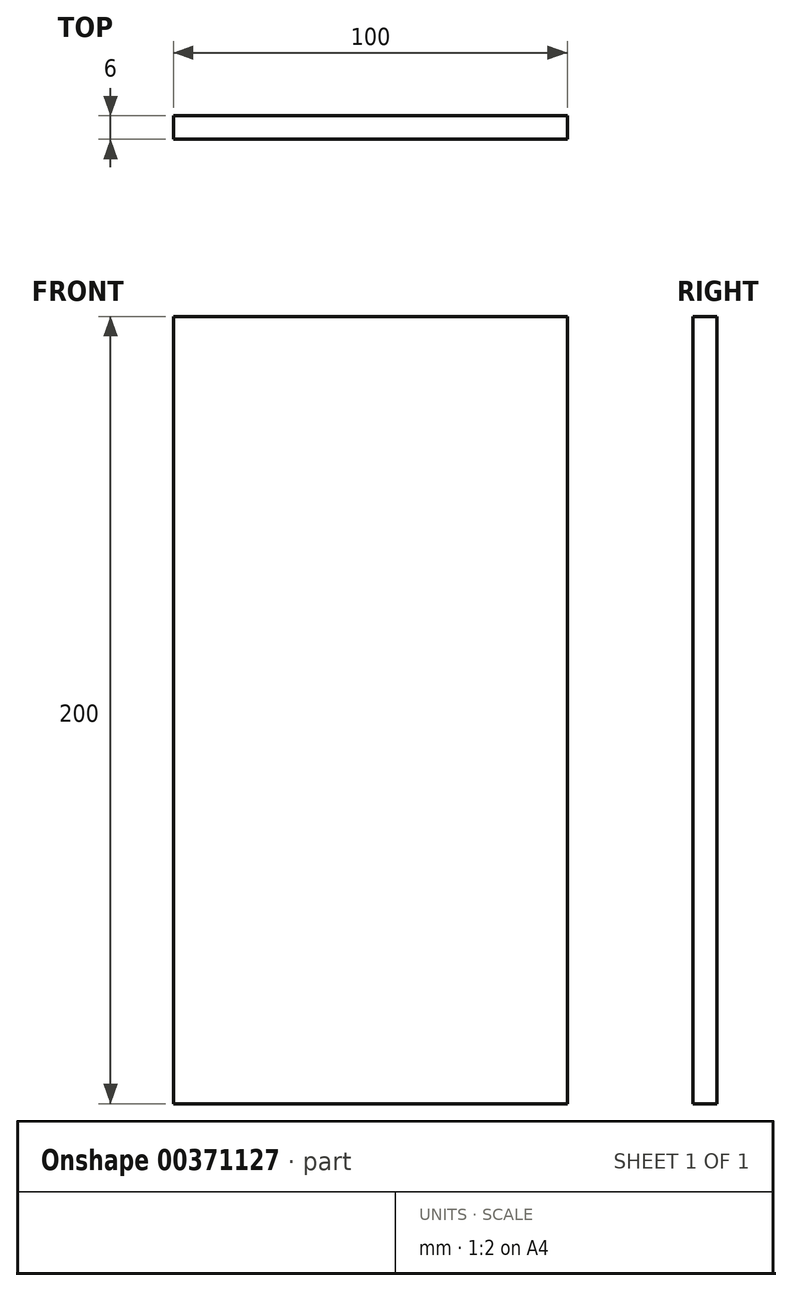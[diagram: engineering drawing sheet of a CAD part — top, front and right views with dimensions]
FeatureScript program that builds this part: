
annotation { "Feature Type Name" : "Feature", "Feature Type Description" : "" }
export const myFeature = defineFeature(function(context is Context, id is Id, definition is map)
    precondition{}
    {
        {
            var Q0;
            Q0=qCreatedBy(makeId("Front.planeOp"),FACE);
            var sketch = newSketch(context, id + "F0", { "sketchPlane" : qUnion([Q0])});
            skLineSegment(sketch, "E0.bottom", {"start": v(50, -100) * mm, "end": v(-50, -100) * mm});
            skLineSegment(sketch, "E0.top", {"start": v(50, 100) * mm, "end": v(-50, 100) * mm});
            skLineSegment(sketch, "E0.left", {"start": v(50, -100) * mm, "end": v(50, 100) * mm});
            skLineSegment(sketch, "E0.right", {"start": v(-50, -100) * mm, "end": v(-50, 100) * mm});
            skPoint(sketch, "E0.middle", {"position": v(0, 0) * mm});
            skSolve(sketch);
        }
        {
            var Q0;
            Q0=makeQuery(id+"F0.imprint","IMPRINT",FACE,{"disambiguationData":[TD([[makeQuery(id+"F0.imprint","IMPRINT",EDGE,{"derivedFrom":sQuery(id+"F0.wireOp",EDGE,"E0.bottom")}),-1.0]])]});
            extrude(context, id + "F1", {"entities" : qUnion([Q0]), "depth" : 6 * mm});
        }
    });
